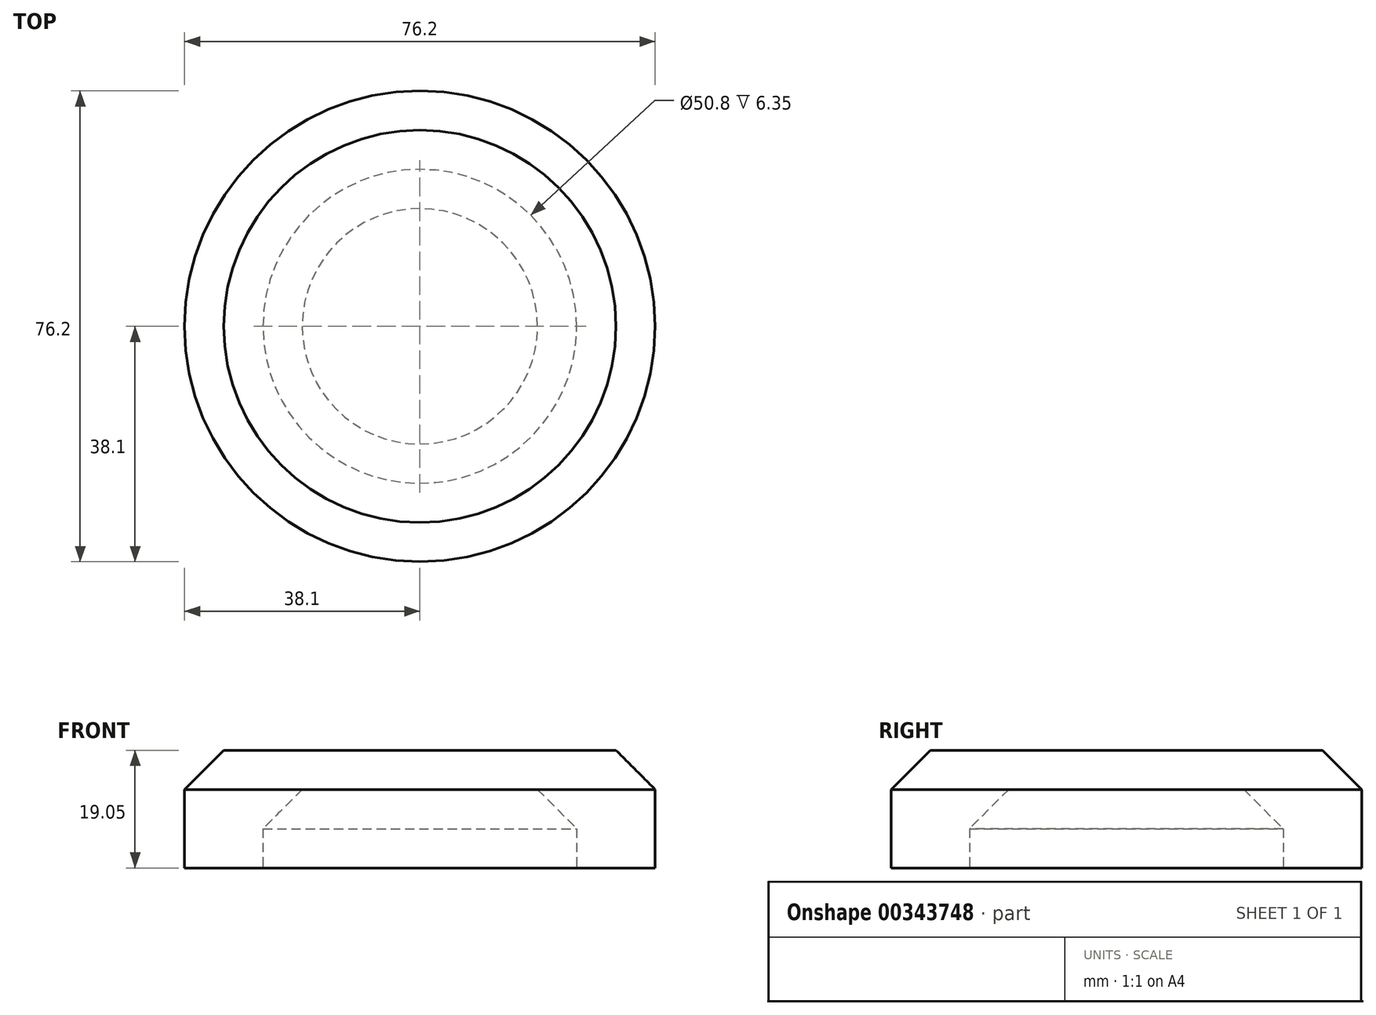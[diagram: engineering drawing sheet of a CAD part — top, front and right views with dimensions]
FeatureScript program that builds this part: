
annotation { "Feature Type Name" : "Feature", "Feature Type Description" : "" }
export const myFeature = defineFeature(function(context is Context, id is Id, definition is map)
    precondition{}
    {
        {
            var Q0;
            Q0=qCreatedBy(makeId("Top.planeOp"),FACE);
            var sketch = newSketch(context, id + "F0", { "sketchPlane" : qUnion([Q0])});
            skCircle(sketch, "E0", {"center": v(0, 0) * mm, "radius": 38.1 * mm});
            skSolve(sketch);
        }
        {
            var Q0;
            Q0 = qSketchRegion(id + "F0", true);
            extrude(context, id + "F1", {"entities" : qUnion([Q0]), "depth" : 19.05 * mm});
        }
        {
            var Q0;
            Q0=makeQuery(id+"F1.opExtrude","CAP_FACE",FACE,{"disambiguationData":[OSD([sQuery(id+"F0.wireOp",EDGE,"E0")])],"isStart":false});
            chamfer(context, id + "F2", {"entities" : qUnion([Q0]), "width" : 6.35 * mm, "tangentPropagation" : true});
        }
        {
            var Q0;
            Q0=makeQuery(id+"F1.opExtrude","CAP_FACE",FACE,{"disambiguationData":[OSD([sQuery(id+"F0.wireOp",EDGE,"E0")])],"isStart":true});
            var sketch = newSketch(context, id + "F3", { "sketchPlane" : qUnion([Q0])});
            skCircle(sketch, "E1", {"center": v(0, 0) * mm, "radius": 25.4 * mm});
            skSolve(sketch);
        }
        {
            var Q0;
            Q0=makeQuery(id+"F3.imprint","IMPRINT",FACE,{"disambiguationData":[TD([[makeQuery(id+"F3.imprint","IMPRINT",EDGE,{"derivedFrom":sQuery(id+"F3.wireOp",EDGE,"E1")}),1.0]])]});
            extrude(context, id + "F4", {"entities" : qUnion([Q0]), "operationType" : NewBodyOperationType.REMOVE, "oppositeDirection" : true, "depth" : 12.7 * mm});
        }
        {
            var Q0;
            Q0=makeQuery(id+"F4.boolean.opBoolean","COPY",FACE,{"derivedFrom":makeQuery(id+"F4.opExtrude","CAP_FACE",FACE,{"disambiguationData":[OSD([sQuery(id+"F3.wireOp",EDGE,"E1")])],"isStart":false})});
            chamfer(context, id + "F5", {"entities" : qUnion([Q0]), "width" : 6.35 * mm, "tangentPropagation" : true});
        }
    });
